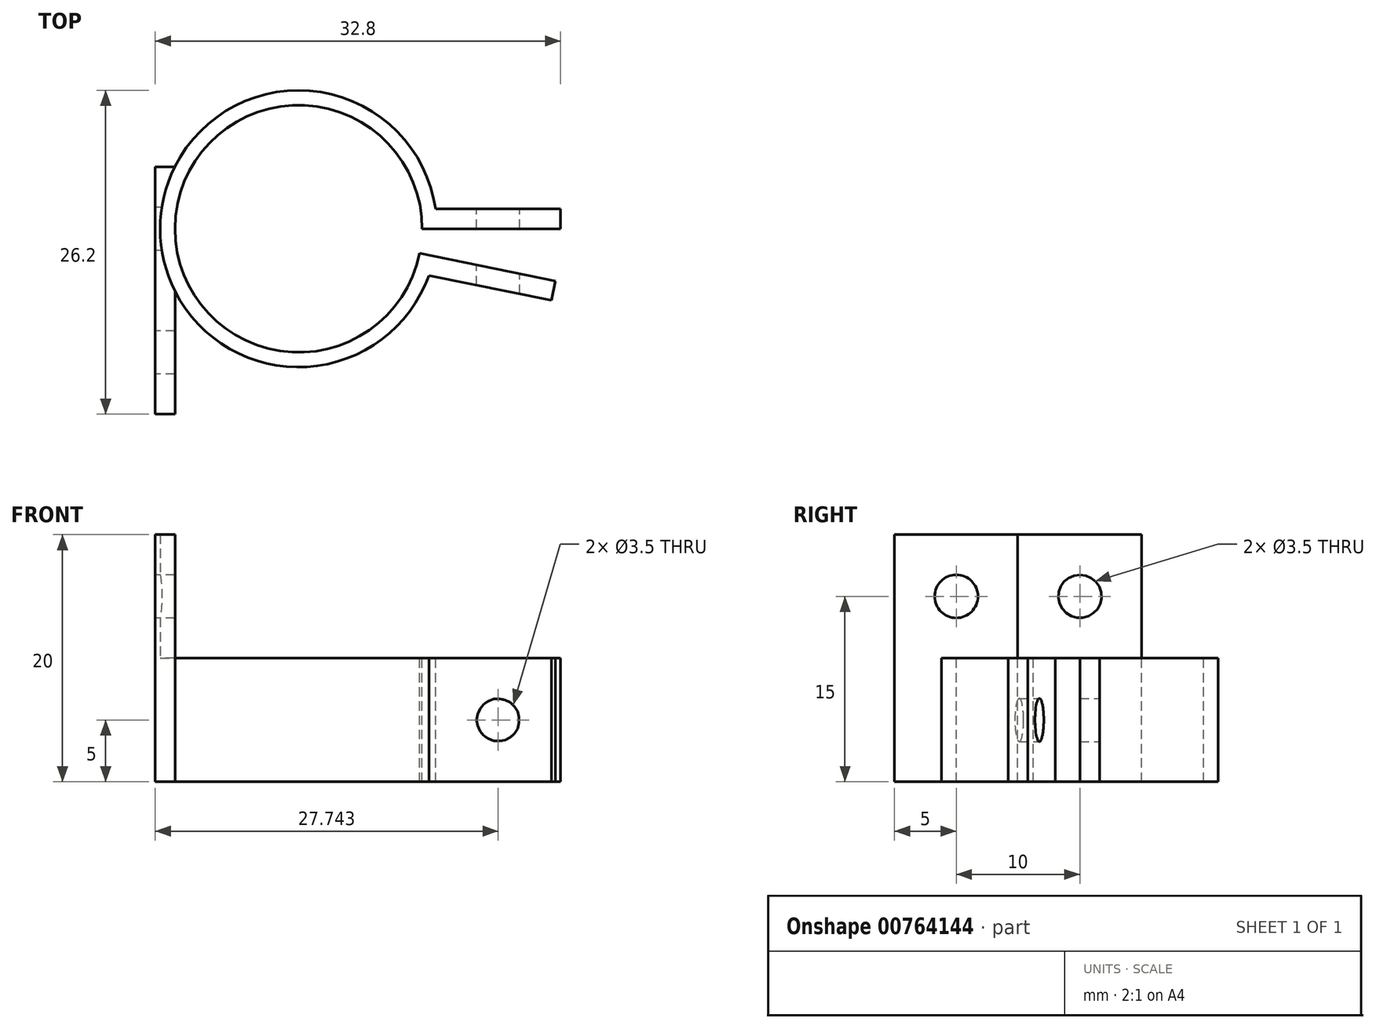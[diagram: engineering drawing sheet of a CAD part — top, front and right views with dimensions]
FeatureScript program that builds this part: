
annotation { "Feature Type Name" : "Feature", "Feature Type Description" : "" }
export const myFeature = defineFeature(function(context is Context, id is Id, definition is map)
    precondition{}
    {
        {
            var Q0;
            Q0=qCreatedBy(makeId("Top.planeOp"),FACE);
            var sketch = newSketch(context, id + "F0", { "sketchPlane" : qUnion([Q0])});
            skArc(sketch, "E0", {"start": v(9.8, -1.99) * mm, "mid": v(-9.95, 1) * mm, "end": v(10, 0) * mm});
            skArc(sketch, "E1", {"start": v(10.98, -2.23) * mm, "mid": v(-11.14, 1.12) * mm, "end": v(11.2, 0) * mm});
            skLineSegment(sketch, "E2", {"start": v(10, 0) * mm, "end": v(11.2, 0) * mm});
            skLineSegment(sketch, "E3", {"start": v(9.8, -1.99) * mm, "end": v(10.98, -2.23) * mm});
            skLineSegment(sketch, "E4", {"start": v(11.2, 0) * mm, "end": v(21.2, 0) * mm});
            skLineSegment(sketch, "E5", {"start": v(21.2, 0) * mm, "end": v(21.2, 1.6) * mm});
            skLineSegment(sketch, "E6", {"start": v(21.2, 1.6) * mm, "end": v(11.09, 1.6) * mm});
            skLineSegment(sketch, "E7", {"start": v(10.98, -2.23) * mm, "end": v(20.78, -4.22) * mm});
            skLineSegment(sketch, "E8", {"start": v(20.78, -4.22) * mm, "end": v(20.46, -5.79) * mm});
            skLineSegment(sketch, "E9", {"start": v(20.46, -5.79) * mm, "end": v(10.55, -3.77) * mm});
            skLineSegment(sketch, "E10.bottom", {"start": v(-11.6, 5) * mm, "end": v(-10, 5) * mm});
            skLineSegment(sketch, "E10.top", {"start": v(-11.6, -15) * mm, "end": v(-10, -15) * mm});
            skLineSegment(sketch, "E10.left", {"start": v(-11.6, 5) * mm, "end": v(-11.6, -15) * mm});
            skLineSegment(sketch, "E10.right", {"start": v(-10, 5) * mm, "end": v(-10, -15) * mm});
            skSolve(sketch);
        }
        {
            var Q0;
            Q0=qSketchRegion(id+"F0",true);
            extrude(context, id + "F1", {"entities" : qUnion([Q0]), "oppositeDirection" : true, "depth" : 10 * mm});
        }
        {
            var Q0;
            {var subQ1=sQuery(id+"F0.wireOp",EDGE,"E10.top");Q0=makeQuery(id+"F0.imprint","IMPRINT",FACE,{"disambiguationData":[TD([[makeQuery(id+"F0.imprint","IMPRINT",EDGE,{"derivedFrom":subQ1}),1.0]])]});}
            var Q1;
            {var subQ0=sQuery(id+"F0.wireOp",EDGE,"E10.right");var subQ1=sQuery(id+"F0.wireOp",EDGE,"E1");var subQ2=makeQuery(id+"F0.imprint","INTERSECT",VERTEX,{"derivedFrom":[subQ1,subQ0]});Q1=makeQuery(id+"F0.imprint","IMPRINT",FACE,{"disambiguationData":[TD([[makeQuery(id+"F0.imprint","IMPRINT",EDGE,{"disambiguationData":[TD([[subQ2,-1.0]])],"derivedFrom":subQ1}),-1.0]])]});}
            extrude(context, id + "F2", {"entities" : qUnion([Q0, Q1]), "operationType" : NewBodyOperationType.ADD, "depth" : 10 * mm});
        }
        {
            var Q0;
            {var subQ0=sQuery(id+"F0.wireOp",EDGE,"E10.left");Q0=makeQuery(id+"F2.boolean.opBoolean","MERGE",FACE,{"derivedFrom":[makeQuery(id+"F1.opExtrude","SWEPT_FACE",FACE,{"disambiguationData":[OSD([subQ0])]}),makeQuery(id+"F2.opExtrude","SWEPT_FACE",FACE,{"disambiguationData":[OSD([subQ0])]})]});}
            var sketch = newSketch(context, id + "F3", { "sketchPlane" : qUnion([Q0])});
            skCircle(sketch, "E11", {"center": v(0, 5) * mm, "radius": 1.75 * mm});
            skCircle(sketch, "E12", {"center": v(10, 5) * mm, "radius": 1.75 * mm});
            skLineSegment(sketch, "E13", {"start": v(0, 5) * mm, "end": v(10, 5) * mm});
            skLineSegment(sketch, "E14", {"start": v(5, 5) * mm, "end": v(5, 10) * mm, "construction": true});
            skSolve(sketch);
        }
        {
            var Q0;
            Q0=qSketchRegion(id+"F3",true);
            extrude(context, id + "F4", {"entities" : qUnion([Q0]), "operationType" : NewBodyOperationType.REMOVE, "oppositeDirection" : true, "depth" : 25 * mm});
        }
        {
            var Q0;
            Q0=makeQuery(id+"F1.opExtrude","SWEPT_FACE",FACE,{"disambiguationData":[OSD([sQuery(id+"F0.wireOp",EDGE,"E6")])]});
            var sketch = newSketch(context, id + "F5", { "sketchPlane" : qUnion([Q0])});
            skLineSegment(sketch, "E15", {"start": v(-11.09, 0) * mm, "end": v(-21.2, -10) * mm, "construction": true});
            skCircle(sketch, "E16", {"center": v(-16.14, -5) * mm, "radius": 1.75 * mm});
            skSolve(sketch);
        }
        {
            var Q0;
            Q0=makeQuery(id+"F5.imprint","IMPRINT",FACE,{"disambiguationData":[TD([[makeQuery(id+"F5.imprint","IMPRINT",EDGE,{"derivedFrom":sQuery(id+"F5.wireOp",EDGE,"E16")}),1.0]])]});
            extrude(context, id + "F6", {"entities" : qUnion([Q0]), "operationType" : NewBodyOperationType.REMOVE, "oppositeDirection" : true, "depth" : 25 * mm});
        }
    });
